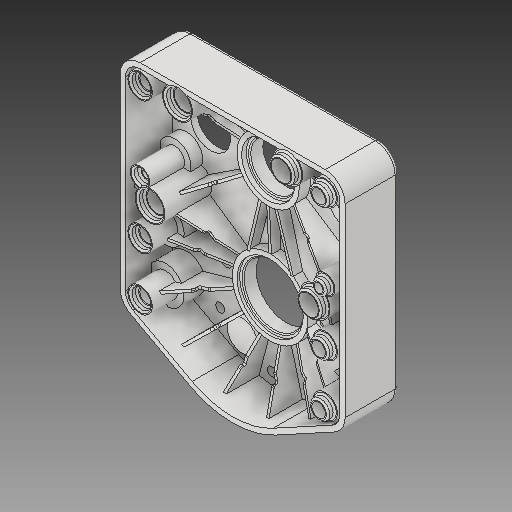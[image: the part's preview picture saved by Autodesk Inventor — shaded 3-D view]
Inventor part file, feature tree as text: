
AUTODESK INVENTOR PART (.ipt)
format: ipt  version: 2017 (Build 210142000, 142)  size: 883,200 bytes
history: native  units: in
note: dims shown in document units (in); Inventor stores cm internally (conversion verified against a paired STEP export)
features: fillet x1
ambient origin geometry x8: Origin, YZ Plane, XZ Plane, XY Plane, X Axis, Y Axis, Z Axis, Center Point
bodies: Solid1 (feature_tree)
feature tree (1):
  fillet  "Fillet18"  [1 undecoded]
note: 1 required parameter value undecoded (feature->parameter linkage not recoverable at this tier; creation-order binding heuristic only, values carry confidence <= 0.55)
